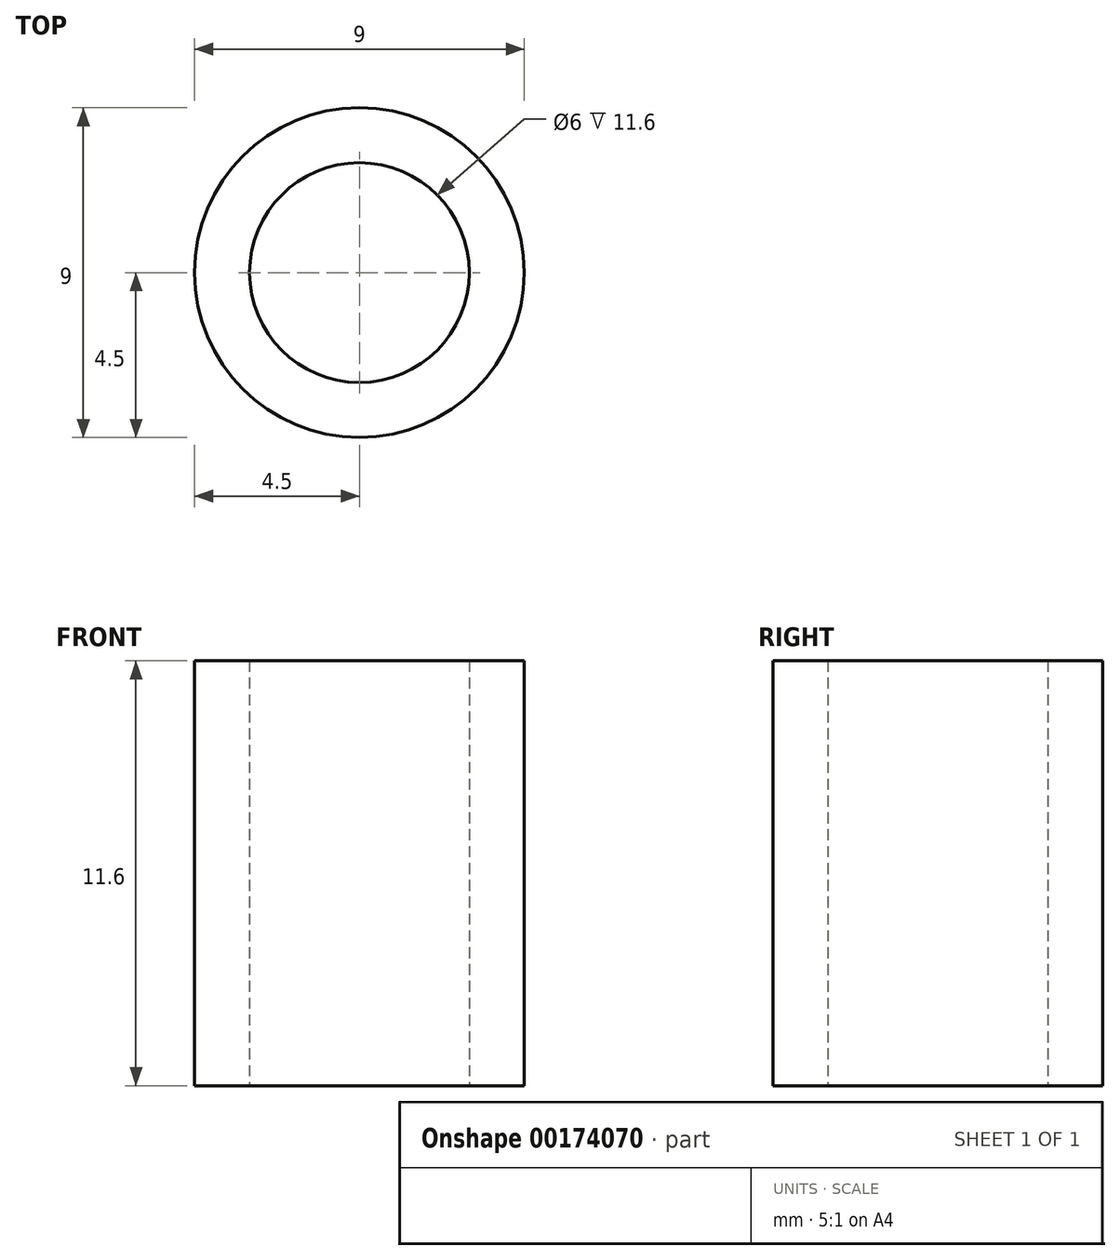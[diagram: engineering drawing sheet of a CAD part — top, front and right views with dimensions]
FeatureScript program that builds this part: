
annotation { "Feature Type Name" : "Feature", "Feature Type Description" : "" }
export const myFeature = defineFeature(function(context is Context, id is Id, definition is map)
    precondition{}
    {
        {
            var Q0;
            Q0=qCreatedBy(makeId("Top.planeOp"),FACE);
            var sketch = newSketch(context, id + "F0", { "sketchPlane" : qUnion([Q0])});
            skCircle(sketch, "E0", {"center": v(0, 0) * mm, "radius": 4.5 * mm});
            skCircle(sketch, "E1", {"center": v(0, 0) * mm, "radius": 3 * mm});
            skSolve(sketch);
        }
        {
            var Q0;
            Q0=makeQuery(id+"F0.imprint","IMPRINT",FACE,{"disambiguationData":[TD([[makeQuery(id+"F0.imprint","IMPRINT",EDGE,{"derivedFrom":sQuery(id+"F0.wireOp",EDGE,"E0")}),1.0]])]});
            extrude(context, id + "F1", {"entities" : qUnion([Q0]), "depth" : 11.6 * mm});
        }
    });
